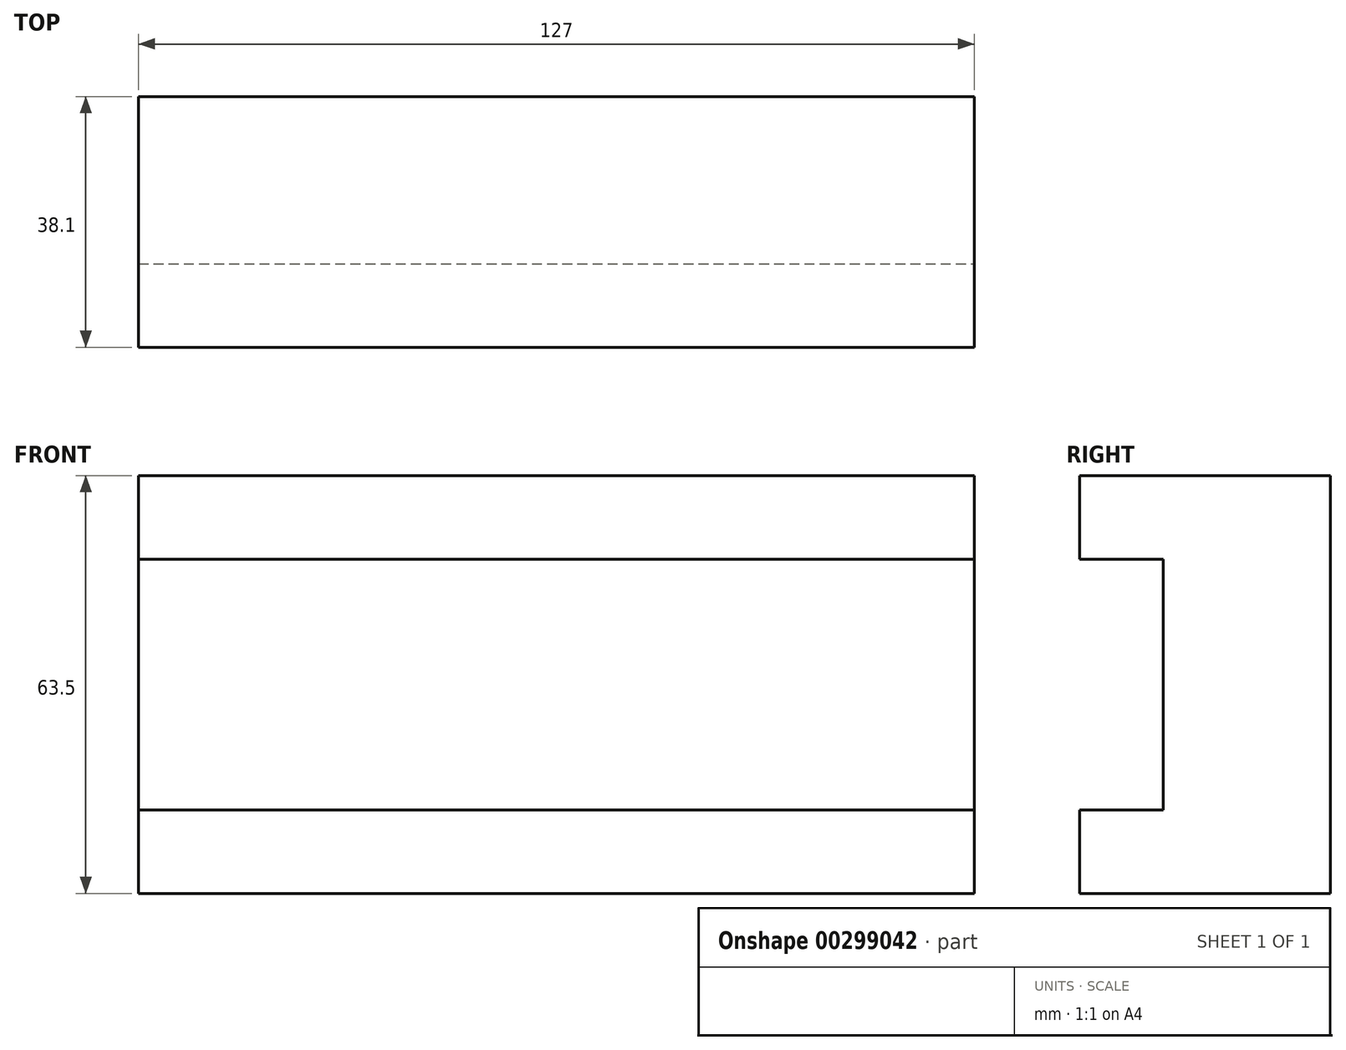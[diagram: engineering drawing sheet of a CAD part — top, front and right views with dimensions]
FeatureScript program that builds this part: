
annotation { "Feature Type Name" : "Feature", "Feature Type Description" : "" }
export const myFeature = defineFeature(function(context is Context, id is Id, definition is map)
    precondition{}
    {
        {
            var Q0;
            Q0=qCreatedBy(makeId("Front.planeOp"),FACE);
            var sketch = newSketch(context, id + "F0", { "sketchPlane" : qUnion([Q0])});
            skLineSegment(sketch, "E0.bottom", {"start": v(-63.5, 31.75) * mm, "end": v(63.5, 31.75) * mm});
            skLineSegment(sketch, "E0.top", {"start": v(-63.5, -31.75) * mm, "end": v(63.5, -31.75) * mm});
            skLineSegment(sketch, "E0.left", {"start": v(-63.5, 31.75) * mm, "end": v(-63.5, -31.75) * mm});
            skLineSegment(sketch, "E0.right", {"start": v(63.5, 31.75) * mm, "end": v(63.5, -31.75) * mm});
            skPoint(sketch, "E0.middle", {"position": v(0, 0) * mm});
            skSolve(sketch);
        }
        {
            var Q0;
            Q0 = qSketchRegion(id + "F0", true);
            extrude(context, id + "F1", {"entities" : qUnion([Q0]), "depth" : 38.1 * mm});
        }
        {
            var Q0;
            Q0=makeQuery(id+"F1.opExtrude","CAP_FACE",FACE,{"disambiguationData":[OSD([sQuery(id+"F0.wireOp",EDGE,"E0.bottom"),sQuery(id+"F0.wireOp",EDGE,"E0.top"),sQuery(id+"F0.wireOp",EDGE,"E0.left"),sQuery(id+"F0.wireOp",EDGE,"E0.right")])],"isStart":false});
            var sketch = newSketch(context, id + "F2", { "sketchPlane" : qUnion([Q0])});
            skLineSegment(sketch, "E1.bottom", {"start": v(-63.5, 25.4) * mm, "end": v(63.5, 25.4) * mm});
            skLineSegment(sketch, "E1.top", {"start": v(-63.5, -25.4) * mm, "end": v(63.5, -25.4) * mm});
            skLineSegment(sketch, "E1.left", {"start": v(-63.5, 25.4) * mm, "end": v(-63.5, -25.4) * mm});
            skLineSegment(sketch, "E1.right", {"start": v(63.5, 25.4) * mm, "end": v(63.5, -25.4) * mm});
            skPoint(sketch, "E1.middle", {"position": v(0, 0) * mm});
            skSolve(sketch);
        }
        {
            var Q0;
            Q0 = qSketchRegion(id + "F2", true);
            extrude(context, id + "F3", {"entities" : qUnion([Q0]), "operationType" : NewBodyOperationType.ADD, "oppositeDirection" : true, "depth" : 12.7 * mm});
        }
        {
            var Q0;
            Q0=makeQuery(id+"F1.opExtrude","SWEPT_FACE",FACE,{"disambiguationData":[OSD([sQuery(id+"F0.wireOp",EDGE,"E0.right")])]});
            var sketch = newSketch(context, id + "F4", { "sketchPlane" : qUnion([Q0])});
            skLineSegment(sketch, "E2.bottom", {"start": v(-38.1, 19.05) * mm, "end": v(-25.4, 19.05) * mm});
            skLineSegment(sketch, "E2.top", {"start": v(-38.1, -19.05) * mm, "end": v(-25.4, -19.05) * mm});
            skLineSegment(sketch, "E2.left", {"start": v(-38.1, 19.05) * mm, "end": v(-38.1, -19.05) * mm});
            skLineSegment(sketch, "E2.right", {"start": v(-25.4, 19.05) * mm, "end": v(-25.4, -19.05) * mm});
            skSolve(sketch);
        }
        {
            var Q0;
            Q0 = qSketchRegion(id + "F4", true);
            extrude(context, id + "F5", {"entities" : qUnion([Q0]), "operationType" : NewBodyOperationType.REMOVE, "endBound" : BoundingType.THROUGH_ALL, "oppositeDirection" : true, "depth" : 25.4 * mm});
        }
    });
